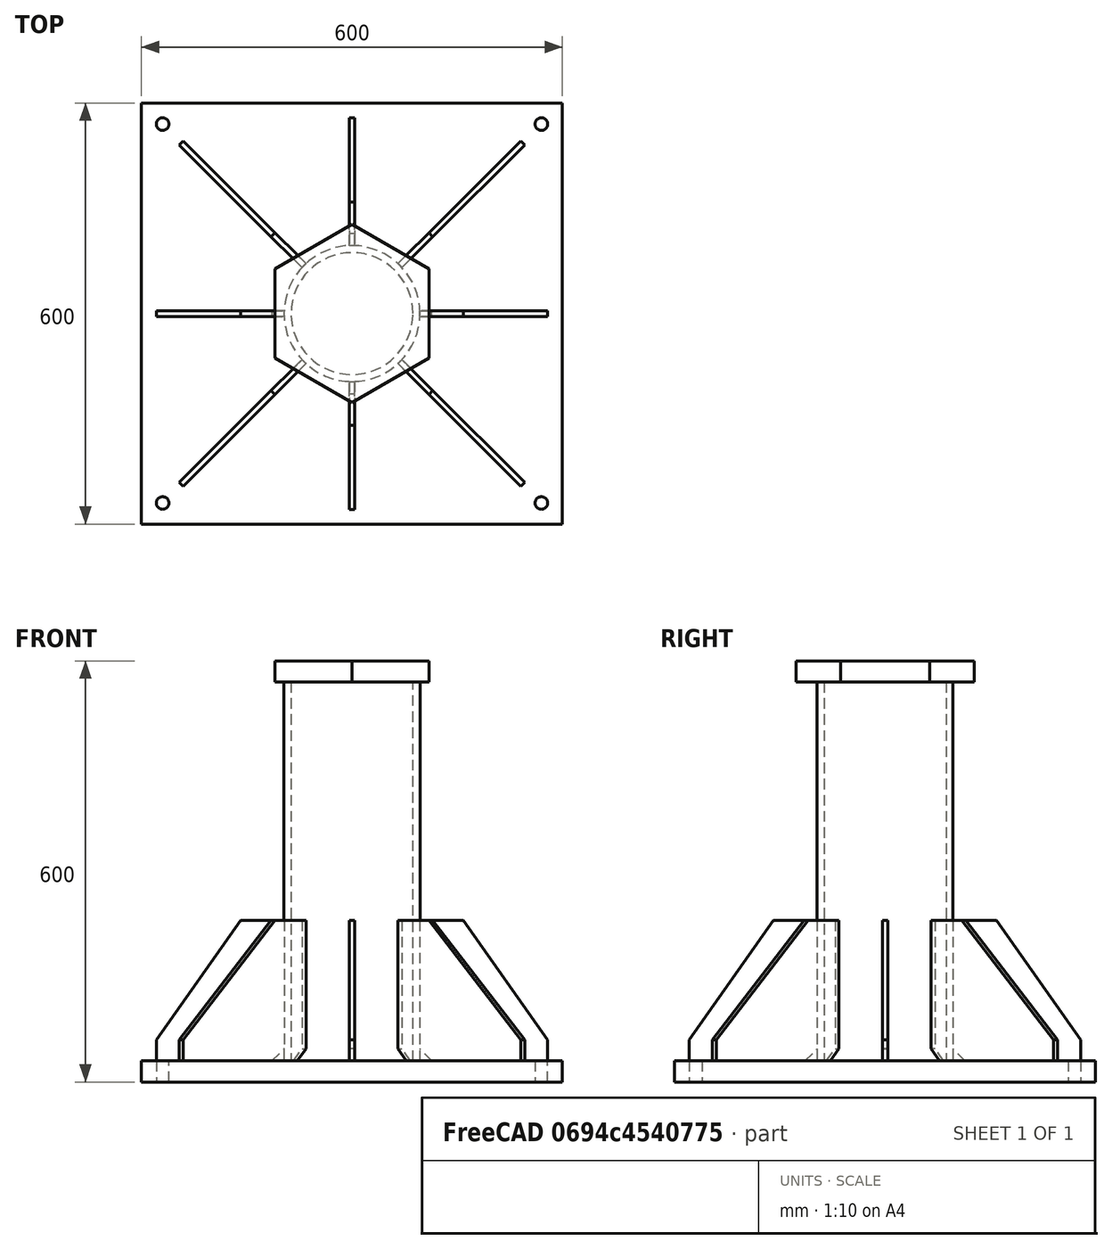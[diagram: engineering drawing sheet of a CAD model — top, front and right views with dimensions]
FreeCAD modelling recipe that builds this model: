
FCSTD DOCUMENT  (FreeCAD 0.21R33771 (Git))
Label: 1310933_Mastverankerung
License: All rights reserved
LicenseURL: http://en.wikipedia.org/wiki/All_rights_reserved
objects: Sketcher::SketchObject×5, Part::Extrusion×5, Fem::ConstraintFixed×4, Fem::ConstraintForce×3, Part::FeaturePython×2, Part::MultiFuse×2, Fem::FemSolverObjectPython×1, App::MaterialObjectPython×1, Fem::FemMeshObjectPython×1, Fem::FemAnalysis×1
note: 14 computed .brp shape members not serialized (recipe doc carries the construction recipe); baked Part::Feature solids carry a one-line shape summary decoded from their .brp

FEATURE [Sketcher::SketchObject] Sketch
  FullyConstrained = true
  sketch-geometry (12):
    g0: LineSegment StartX=-300 StartY=300 StartZ=0 EndX=300 EndY=300 EndZ=0
    g1: LineSegment StartX=300 StartY=300 StartZ=0 EndX=300 EndY=-300 EndZ=0
    g2: LineSegment StartX=300 StartY=-300 StartZ=0 EndX=-300 EndY=-300 EndZ=0
    g3: LineSegment StartX=-300 StartY=-300 StartZ=0 EndX=-300 EndY=300 EndZ=0
    g4: LineSegment StartX=-270 StartY=270 StartZ=0 EndX=270 EndY=270 EndZ=0
    g5: LineSegment StartX=270 StartY=270 StartZ=0 EndX=270 EndY=-270 EndZ=0
    g6: LineSegment StartX=270 StartY=-270 StartZ=0 EndX=-270 EndY=-270 EndZ=0
    g7: LineSegment StartX=-270 StartY=-270 StartZ=0 EndX=-270 EndY=270 EndZ=0
    g8: Circle CenterX=270 CenterY=-270 CenterZ=0 NormalX=0 NormalY=0 NormalZ=1 AngleXU=0 Radius=9
    g9: Circle CenterX=-270 CenterY=-270 CenterZ=0 NormalX=0 NormalY=0 NormalZ=1 AngleXU=0 Radius=9
    g10: Circle CenterX=270 CenterY=270 CenterZ=0 NormalX=0 NormalY=0 NormalZ=1 AngleXU=0 Radius=9
    g11: Circle CenterX=-270 CenterY=270 CenterZ=0 NormalX=0 NormalY=0 NormalZ=1 AngleXU=0 Radius=9
  constraints (28):
    c: Coincident(g0,g1)
    c: Coincident(g1,g2)
    c: Coincident(g2,g3)
    c: Coincident(g3,g0)
    c: Horizontal(g0)
    c: Vertical(g1)
    c: Symmetric(g2,g1,g-2)
    c: Symmetric(g2,g0,g-1)
    c: Equal(g2,g3)
    c: DistanceX(g2,g2) = 600
    c: Coincident(g4,g5)
    c: Coincident(g5,g6)
    c: Coincident(g6,g7)
    c: Coincident(g7,g4)
    c: Horizontal(g4)
    c: Vertical(g5)
    c: Symmetric(g6,g5,g-2)
    c: Symmetric(g6,g4,g-1)
    c: Equal(g6,g7)
    c: DistanceX(g6,g6) = 540
    c: Coincident(g8,g5)
    c: Coincident(g9,g6)
    c: Coincident(g10,g4)
    c: Coincident(g11,g4)
    c: Equal(g11,g10)
    c: Equal(g11,g9)
    c: Equal(g11,g8)
    c: Diameter(g11) = 18
FEATURE [Part::Extrusion] Extrude  label="platte"
  Base = -> Sketch
  Dir = (0,0,1)
  DirMode = 0
  FaceMakerClass = Part::FaceMakerBullseye
  LengthFwd = 30
  LengthRev = 0
  Solid = true
  Symmetric = false
FEATURE [Sketcher::SketchObject] Sketch001
  FullyConstrained = true
  MapMode = 5
  Placement = pos=(0,0,30) rot=(0,0,1;0rad)
  Support = -> [Extrude]
  sketch-geometry (3):
    g0: Circle CenterX=6e-16 CenterY=0 CenterZ=0 NormalX=0 NormalY=0 NormalZ=1 AngleXU=0 Radius=96.85
    g1: Circle CenterX=6e-16 CenterY=0 CenterZ=0 NormalX=0 NormalY=0 NormalZ=1 AngleXU=0 Radius=86.85
    g2: LineSegment StartX=86.85 StartY=0 StartZ=0 EndX=96.85 EndY=0 EndZ=0
  constraints (8):
    c: Coincident(g0,g-1)
    c: Coincident(g1,g0)
    c: PointOnObject(g2,g1)
    c: PointOnObject(g2,g0)
    c: PointOnObject(g2,g-1)
    c: Horizontal(g2)
    c: Diameter(g0) = 193.7
    c: DistanceX(g2,g2) = 10
FEATURE [Part::Extrusion] Extrude001  label="rohr"
  Base = -> Sketch001
  Dir = (0,0,1)
  DirMode = 2
  FaceMakerClass = Part::FaceMakerBullseye
  LengthFwd = 540
  LengthRev = 0
  Solid = true
  Symmetric = false
FEATURE [Sketcher::SketchObject] Sketch002
  ExternalGeometry = -> [Extrude]
  FullyConstrained = true
  Placement = pos=(0,0,0) rot=(1,0,0;1.5708rad)
  sketch-geometry (6):
    g0: LineSegment StartX=114 StartY=30 StartZ=0 EndX=94 EndY=50 EndZ=0
    g1: LineSegment StartX=94 StartY=50 StartZ=0 EndX=94 EndY=230 EndZ=0
    g2: LineSegment StartX=94 StartY=230 StartZ=0 EndX=159 EndY=230 EndZ=0
    g3: LineSegment StartX=159 StartY=230 StartZ=0 EndX=279 EndY=60 EndZ=0
    g4: LineSegment StartX=279 StartY=60 StartZ=0 EndX=279 EndY=30 EndZ=0
    g5: LineSegment StartX=279 StartY=30 StartZ=0 EndX=114 EndY=30 EndZ=0
  constraints (18):
    c: Coincident(g0,g1)
    c: Vertical(g1)
    c: Coincident(g1,g2)
    c: Horizontal(g2)
    c: Coincident(g2,g3)
    c: Coincident(g3,g4)
    c: Vertical(g4)
    c: Coincident(g4,g5)
    c: Coincident(g5,g0)
    c: Horizontal(g5)
    c: Horizontal(g4,g-3)
    c: Angle(g5,g0) = 2.35619
    c: DistanceX(g-1,g0) = 94
    c: DistanceX(g0,g4) = 185
    c: DistanceX(g0,g0) = 20
    c: DistanceY(g0,g1) = 200
    c: DistanceY(g4,g4) = 30
    c: DistanceX(g2,g2) = 65
FEATURE [Part::Extrusion] Extrude002
  Base = -> Sketch002
  Dir = (0,1,0)
  DirMode = 0
  FaceMakerClass = Part::FaceMakerBullseye
  LengthFwd = 8
  LengthRev = 0
  Solid = true
  Symmetric = true
FEATURE [Part::FeaturePython] Array  label="steife7"  # Draft array (typed FeaturePython)
  Angle = 360
  ArrayType = 1
  Axis = (0,0,1)
  Base = -> Extrude002
  Center = (0,0,0)
  Count = 4
  Fuse = false
  IntervalAxis = (0,0,0)
  IntervalX = (50,0,0)
  IntervalY = (0,50,0)
  IntervalZ = (0,0,50)
  NumberCircles = 3
  NumberPolar = 4
  NumberX = 2
  NumberY = 2
  NumberZ = 1
  RadialDistance = 50
  Symmetry = 1
  TangentialDistance = 25
FEATURE [Sketcher::SketchObject] Sketch003
  ExternalGeometry = -> [Extrude]
  FullyConstrained = true
  Placement = pos=(0,0,0) rot=(1,0,0;1.5708rad)
  sketch-geometry (6):
    g0: LineSegment StartX=114 StartY=30 StartZ=0 EndX=94 EndY=50 EndZ=0
    g1: LineSegment StartX=94 StartY=50 StartZ=0 EndX=94 EndY=230 EndZ=0
    g2: LineSegment StartX=94 StartY=230 StartZ=0 EndX=159 EndY=230 EndZ=0
    g3: LineSegment StartX=159 StartY=230 StartZ=0 EndX=344 EndY=60 EndZ=0
    g4: LineSegment StartX=344 StartY=60 StartZ=0 EndX=344 EndY=30 EndZ=0
    g5: LineSegment StartX=344 StartY=30 StartZ=0 EndX=114 EndY=30 EndZ=0
  constraints (18):
    c: Coincident(g0,g1)
    c: Vertical(g1)
    c: Coincident(g1,g2)
    c: Horizontal(g2)
    c: Coincident(g2,g3)
    c: Coincident(g3,g4)
    c: Vertical(g4)
    c: Coincident(g4,g5)
    c: Coincident(g5,g0)
    c: Horizontal(g5)
    c: Horizontal(g4,g-3)
    c: DistanceX(g-1,g0) = 94
    c: Angle(g5,g0) = 2.35619
    c: DistanceX(g0,g0) = 20
    c: DistanceY(g0,g1) = 200
    c: DistanceY(g4,g4) = 30
    c: DistanceX(g2,g2) = 65
    c: DistanceX(g0,g4) = 250
FEATURE [Part::Extrusion] Extrude003
  Base = -> Sketch003
  Dir = (0,-1,-3e-16)
  DirMode = 2
  FaceMakerClass = Part::FaceMakerBullseye
  LengthFwd = 8
  LengthRev = 0
  Solid = true
  Symmetric = true
FEATURE [Part::FeaturePython] Array001  label="steife8"  # Draft array (typed FeaturePython)
  Angle = 360
  ArrayType = 1
  Axis = (0,0,1)
  Base = -> Extrude003
  Center = (0,0,0)
  Count = 4
  Fuse = false
  IntervalAxis = (0,0,0)
  IntervalX = (50,0,0)
  IntervalY = (0,50,0)
  IntervalZ = (0,0,50)
  NumberCircles = 3
  NumberPolar = 4
  NumberX = 2
  NumberY = 2
  NumberZ = 1
  Placement = pos=(0,0,0) rot=(0,0,1;0.785398rad)
  RadialDistance = 50
  Symmetry = 1
  TangentialDistance = 25
FEATURE [Part::MultiFuse] Fusion
  Refine = true
  Shapes = -> [Extrude,Extrude001,Array,Array001]
FEATURE [Sketcher::SketchObject] Sketch004
  ExternalGeometry = -> [Fusion]
  FullyConstrained = true
  MapMode = 5
  Placement = pos=(0,0,570) rot=(0,0,1;0rad)
  Support = -> [Fusion]
  sketch-geometry (7):
    g0: LineSegment StartX=110 StartY=63.5085 StartZ=0 EndX=1.42e-14 EndY=127.017 EndZ=0
    g1: LineSegment StartX=1.42e-14 StartY=127.017 StartZ=0 EndX=-110 EndY=63.5085 EndZ=0
    g2: LineSegment StartX=-110 StartY=63.5085 StartZ=0 EndX=-110 EndY=-63.5085 EndZ=0
    g3: LineSegment StartX=-110 StartY=-63.5085 StartZ=0 EndX=2.84e-14 EndY=-127.017 EndZ=0
    g4: LineSegment StartX=2.84e-14 StartY=-127.017 StartZ=0 EndX=110 EndY=-63.5085 EndZ=0
    g5: LineSegment StartX=110 StartY=-63.5085 StartZ=0 EndX=110 EndY=63.5085 EndZ=0
    g6: Circle CenterX=6e-16 CenterY=0 CenterZ=0 NormalX=0 NormalY=0 NormalZ=1 AngleXU=0 Radius=127.017
  constraints (16):
    c: Coincident(g0,g1)
    c: Coincident(g1,g2)
    c: Coincident(g2,g3)
    c: Coincident(g3,g4)
    c: Coincident(g4,g5)
    c: Coincident(g5,g0)
    c: Equal(g0, g1-g5) x5
    c: PointOnObject(g0,g6)
    c: PointOnObject(g1,g6)
    c: PointOnObject(g2,g6)
    c: PointOnObject(g3,g6)
    c: PointOnObject(g4,g6)
    c: PointOnObject(g5,g6)
    c: Coincident(g6,g-3)
    c: Vertical(g5)
    c: DistanceX(g1,g0) = 220
FEATURE [Part::Extrusion] Extrude004  label="lastplatte"
  Base = -> Sketch004
  Dir = (0,0,1)
  DirMode = 2
  FaceMakerClass = Part::FaceMakerBullseye
  LengthFwd = 30
  LengthRev = 0
  Solid = true
  Symmetric = false
FEATURE [Part::MultiFuse] Fusion001
  Refine = true
  Shapes = -> [Fusion,Extrude004]
FEATURE [Fem::FemSolverObjectPython] SolverCcxTools  # FEM object (typed FeaturePython)
  AnalysisType = 0
  BeamShellResultOutput3D = true
  BucklingFactors = 1
  EigenmodeHighLimit = 1000000
  EigenmodeLowLimit = 0
  EigenmodesCount = 10
  GeometricalNonlinearity = 0
  IterationsControlParameterCutb = 0.25,0.5,0.75,0.85,,,1.5,
  IterationsControlParameterIter = 4,8,9,200,10,400,,200,,
  IterationsControlParameterTimeUse = false
  IterationsThermoMechMaximum = 2000
  IterationsUserDefinedIncrementations = false
  IterationsUserDefinedTimeStepLength = false
  MaterialNonlinearity = 0
  MatrixSolverType = 0
  SplitInputWriter = true
  ThermoMechSteadyState = true
  TimeEnd = 1
  TimeInitialStep = 0.01
FEATURE [App::MaterialObjectPython] MaterialSolid  label="S235"  # material (typed FeaturePython)
  Category = 0
  Material = AuthorAndLicense=(c) 2013 Juergen Riegel (CC-BY 3.0),CardName=CalculiX-Steel,Density=7900 kg/m^3,+8 more (map truncated)
FEATURE [Fem::ConstraintFixed] ConstraintFixed
  NormalDirection = (1,-1e-16,0)
  Normals = (16) [(-1,0,0),(0.5,-0.866025,0),(0.5,0.866025,0),(-1,2.44929e-16,0),(-1,0,0),(0.5,-0.866025,0),(0.5,0.866025,0),(-1,2.44929e-16,0),(-1,0,0),+7 more]
  Points = (16) [(-261,-270,30),(-274.5,-262.206,30),(-274.5,-277.794,30),(-261,-270,30),(-261,-270,20),(-274.5,-262.206,20),(-274.5,-277.794,20),(-261,-270,20),+8 more]
  References = -> [Fusion001]
  Scale = 5
FEATURE [Fem::ConstraintFixed] ConstraintFixed001
  NormalDirection = (1,-1e-16,0)
  Normals = (16) [(-1,0,0),(0.5,-0.866025,0),(0.5,0.866025,0),(-1,2.44929e-16,0),(-1,0,0),(0.5,-0.866025,0),(0.5,0.866025,0),(-1,2.44929e-16,0),(-1,0,0),+7 more]
  Points = (16) [(-261,270,30),(-274.5,277.794,30),(-274.5,262.206,30),(-261,270,30),(-261,270,20),(-274.5,277.794,20),(-274.5,262.206,20),(-261,270,20),(-261,270,10),+7 more]
  References = -> [Fusion001]
  Scale = 5
FEATURE [Fem::ConstraintFixed] ConstraintFixed002
  NormalDirection = (1,-1e-16,0)
  Normals = (16) [(-1,0,0),(0.5,-0.866025,0),(0.5,0.866025,0),(-1,2.44929e-16,0),(-1,0,0),(0.5,-0.866025,0),(0.5,0.866025,0),(-1,2.44929e-16,0),(-1,0,0),+7 more]
  Points = (16) [(279,270,30),(265.5,277.794,30),(265.5,262.206,30),(279,270,30),(279,270,20),(265.5,277.794,20),(265.5,262.206,20),(279,270,20),(279,270,10),+7 more]
  References = -> [Fusion001]
  Scale = 5
FEATURE [Fem::ConstraintFixed] ConstraintFixed003
  NormalDirection = (1,-1e-16,0)
  Normals = (16) [(-1,0,0),(0.5,-0.866025,0),(0.5,0.866025,0),(-1,2.44929e-16,0),(-1,0,0),(0.5,-0.866025,0),(0.5,0.866025,0),(-1,2.44929e-16,0),(-1,0,0),+7 more]
  Points = (16) [(279,-270,30),(265.5,-262.206,30),(265.5,-277.794,30),(279,-270,30),(279,-270,20),(265.5,-262.206,20),(265.5,-277.794,20),(279,-270,20),(279,-270,10),+7 more]
  References = -> [Fusion001]
  Scale = 5
FEATURE [Fem::ConstraintForce] ConstraintForce  label="H"
  Direction = -> Fusion001 [Edge60]
  DirectionVector = (1,0,0)
  Force = 4710
  NormalDirection = (0,0,1)
  Points = (8) [(-110,-42.339,600),(-36.6667,-42.339,600),(36.6667,-42.339,600),(110,-42.339,600),(-110,42.339,600),(-36.6667,42.339,600),(36.6667,42.339,600),+1 more]
  References = -> [Fusion001]
  Reversed = true
  Scale = 16
FEATURE [Fem::ConstraintForce] ConstraintForce001  label="V1"
  Direction = -> Fusion001 [Edge18]
  DirectionVector = (0,0,-1)
  Force = 98000
  NormalDirection = (1,0,0)
  Points = (16) [(110,-63.5085,600),(110,-21.1695,600),(110,21.1695,600),(110,63.5085,600),(110,-63.5085,590),(110,-21.1695,590),(110,21.1695,590),(110,63.5085,590),+8 more]
  References = -> [Fusion001]
  Reversed = true
  Scale = 8
FEATURE [Fem::ConstraintForce] ConstraintForce002  label="V2"
  Direction = -> Fusion001 [Edge18]
  DirectionVector = (0,0,1)
  Force = 98000
  NormalDirection = (-1,6e-16,0)
  Points = (16) [(-110,63.5085,600),(-110,21.1695,600),(-110,-21.1695,600),(-110,-63.5085,600),(-110,63.5085,590),(-110,21.1695,590),(-110,-21.1695,590),+9 more]
  References = -> [Fusion001]
  Scale = 8
FEATURE [Fem::FemMeshObjectPython] FEMMeshGmsh  # FEM object (typed FeaturePython)
  Algorithm2D = 0
  Algorithm3D = 0
  CharacteristicLengthMax = 10
  CharacteristicLengthMin = 0
  CoherenceMesh = true
  ElementDimension = 3
  ElementOrder = 1
  GeometryTolerance = 1e-06
  GroupsOfNodes = false
  HighOrderOptimize = 0
  MeshSizeFromCurvature = 12
  OptimizeNetgen = false
  OptimizeStd = true
  Part = -> Fusion001
  RecombinationAlgorithm = 0
  Recombine3DAll = false
  RecombineAll = false
  SecondOrderLinear = false
FEATURE [Fem::FemAnalysis] Analysis
  Group = -> [SolverCcxTools,MaterialSolid,ConstraintFixed,ConstraintFixed001,ConstraintFixed002,ConstraintFixed003,ConstraintForce,ConstraintForce001,ConstraintForce002,FEMMeshGmsh]
